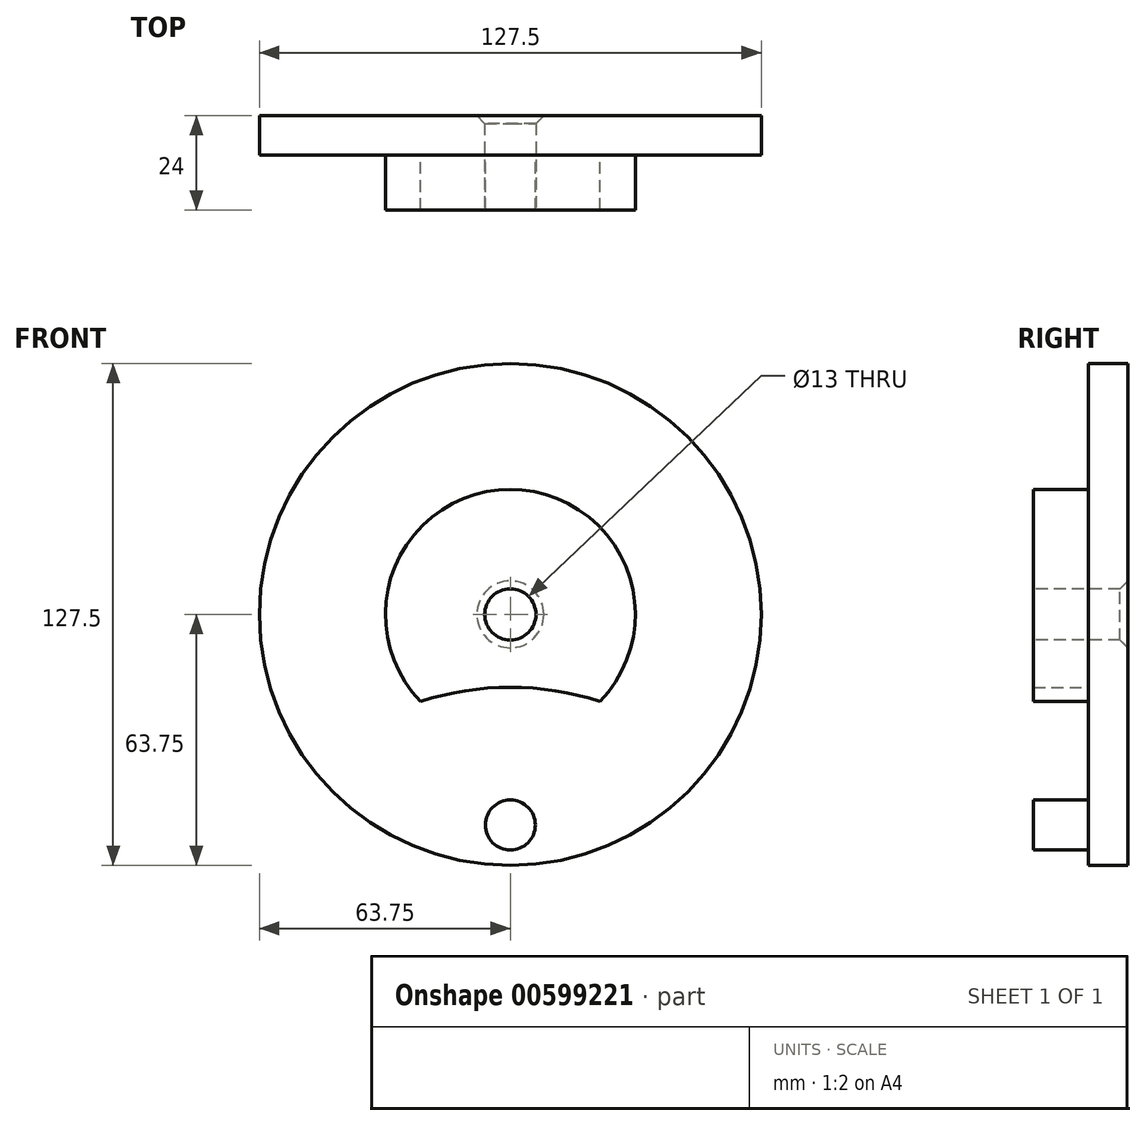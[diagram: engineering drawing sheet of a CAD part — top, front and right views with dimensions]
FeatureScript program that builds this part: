
annotation { "Feature Type Name" : "Feature", "Feature Type Description" : "" }
export const myFeature = defineFeature(function(context is Context, id is Id, definition is map)
    precondition{}
    {
        {
            var Q0;
            Q0=qCreatedBy(makeId("Front.planeOp"),FACE);
            var sketch = newSketch(context, id + "F0", { "sketchPlane" : qUnion([Q0])});
            skCircle(sketch, "E0", {"center": v(0, 0) * mm, "radius": 6.35 * mm, "construction": true});
            skCircle(sketch, "E1", {"center": v(0, 0) * mm, "radius": 31.75 * mm, "construction": true});
            skCircle(sketch, "E2", {"center": v(0, -92) * mm, "radius": 73 * mm, "construction": true});
            skLineSegment(sketch, "E3", {"start": v(0, -92) * mm, "end": v(36.5, -28.78) * mm, "construction": true});
            skCircle(sketch, "E4", {"center": v(0, -53.5) * mm, "radius": 6.35 * mm, "construction": true});
            skSolve(sketch);
        }
        {
            var Q0;
            Q0=qCreatedBy(makeId("Front.planeOp"),FACE);
            var sketch = newSketch(context, id + "F1", { "sketchPlane" : qUnion([Q0])});
            skCircle(sketch, "E5", {"center": v(0, 0) * mm, "radius": 63.75 * mm});
            skSolve(sketch);
        }
        {
            var Q0;
            Q0 = qSketchRegion(id + "F1", true);
            extrude(context, id + "F2", {"entities" : qUnion([Q0]), "oppositeDirection" : true, "depth" : 10 * mm, "offsetDistance" : 25 * mm});
        }
        {
            var Q0;
            Q0=qCreatedBy(makeId("Front.planeOp"),FACE);
            var sketch = newSketch(context, id + "F3", { "sketchPlane" : qUnion([Q0])});
            skArc(sketch, "E6", {"start": v(22.78, -22.12) * mm, "mid": v(0, 31.75) * mm, "end": v(-22.78, -22.12) * mm});
            skArc(sketch, "E7", {"start": v(22.78, -22.12) * mm, "mid": v(0, -18.5) * mm, "end": v(-22.78, -22.12) * mm});
            skCircle(sketch, "E8", {"center": v(0, -53.5) * mm, "radius": 6.35 * mm});
            skSolve(sketch);
        }
        {
            var Q0;
            Q0 = qSketchRegion(id + "F3", true);
            extrude(context, id + "F4", {"entities" : qUnion([Q0]), "operationType" : NewBodyOperationType.ADD, "depth" : 14 * mm, "offsetDistance" : 25 * mm});
        }
        {
            var Q0;
            Q0=qCreatedBy(makeId("Front.planeOp"),FACE);
            var sketch = newSketch(context, id + "F5", { "sketchPlane" : qUnion([Q0])});
            skCircle(sketch, "E9", {"center": v(0, 0) * mm, "radius": 6.5 * mm});
            skSolve(sketch);
        }
        {
            var Q0;
            Q0 = qSketchRegion(id + "F5", true);
            extrude(context, id + "F6", {"entities" : qUnion([Q0]), "operationType" : NewBodyOperationType.REMOVE, "endBound" : BoundingType.THROUGH_ALL, "oppositeDirection" : true, "depth" : 25 * mm, "offsetDistance" : 25 * mm, "hasSecondDirection" : true, "secondDirectionBound" : SecondDirectionBoundingType.THROUGH_ALL, "secondDirectionOppositeDirection" : false, "secondDirectionDepth" : 25 * mm});
        }
        {
            var Q0;
            Q0=makeQuery(id+"F6.boolean.opBoolean","INTERSECT",EDGE,{"derivedFrom":[makeQuery(id+"F2.opExtrude","CAP_FACE",FACE,{"disambiguationData":[OSD([sQuery(id+"F1.wireOp",EDGE,"E5")])],"isStart":false}),makeQuery(id+"F6.opExtrude","SWEPT_FACE",FACE,{"disambiguationData":[OSD([sQuery(id+"F5.wireOp",EDGE,"E9")])]})]});
            chamfer(context, id + "F7", {"entities" : qUnion([Q0]), "width" : 2 * mm, "tangentPropagation" : true});
        }
    });
